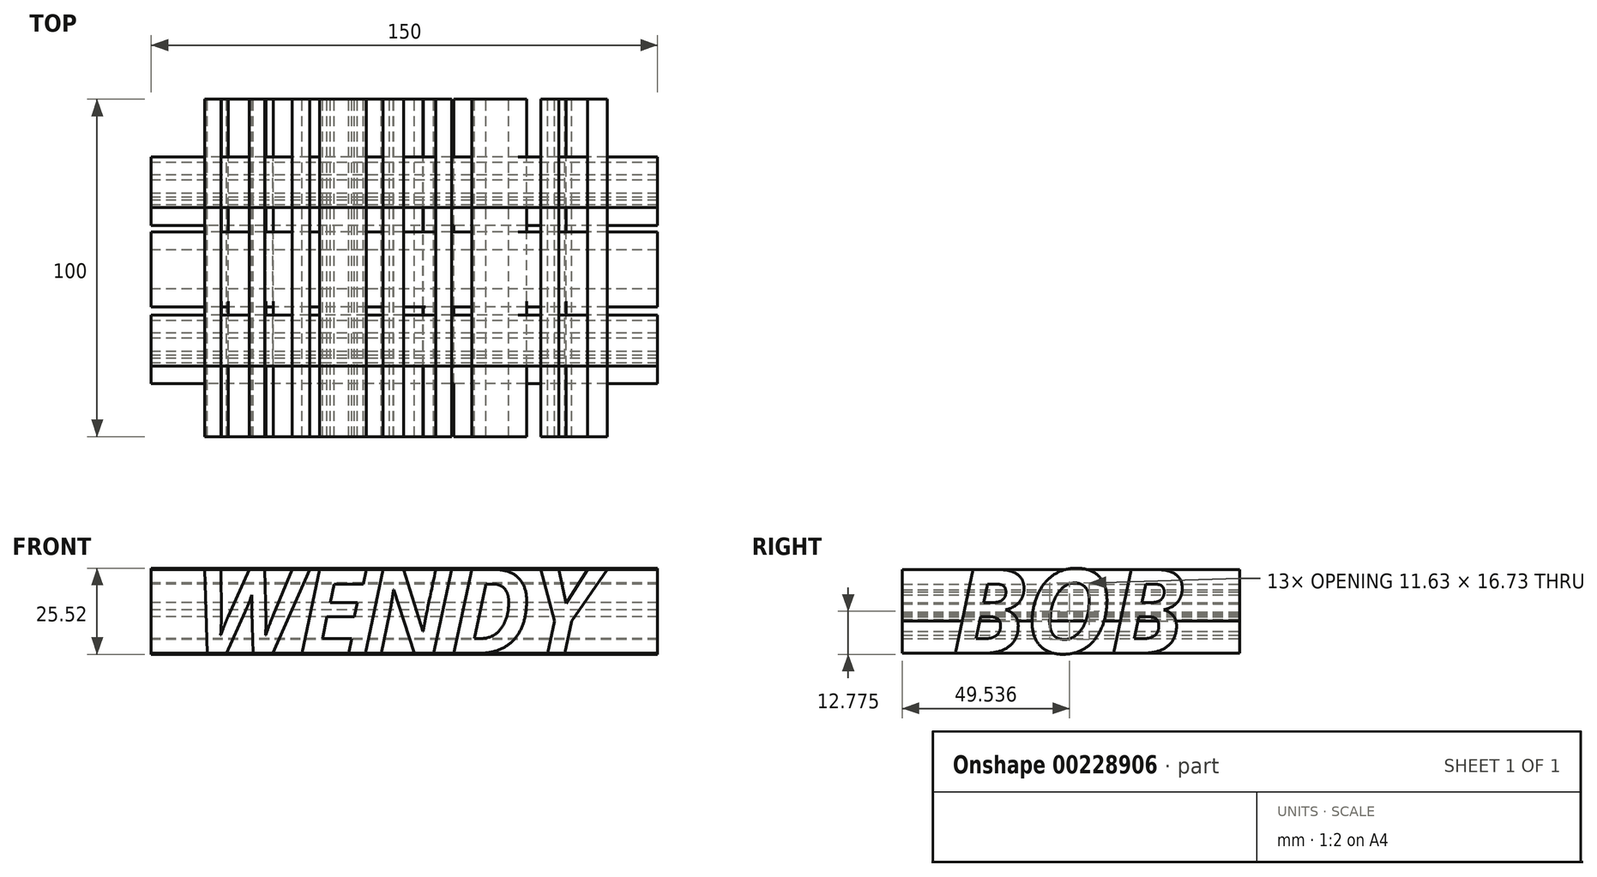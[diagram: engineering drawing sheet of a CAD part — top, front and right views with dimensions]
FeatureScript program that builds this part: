
annotation { "Feature Type Name" : "Feature", "Feature Type Description" : "" }
export const myFeature = defineFeature(function(context is Context, id is Id, definition is map)
    precondition{}
    {
        {
            var Q0;
            Q0=qCreatedBy(makeId("Front.planeOp"),FACE);
            var sketch = newSketch(context, id + "F0", { "sketchPlane" : qUnion([Q0])});
            skText(sketch, "E0", { "text": "WENDY", "fontName": "OpenSans-BoldItalic.ttf"});
            skCircle(sketch, "E1", {"center": v(57.85, 11.4) * mm, "radius": 1.86 * mm});
            const initialGuessF0  = {"E0": [-0.0623, 0, 1, 0, 0.025]};
            skSetInitialGuess(sketch, initialGuessF0);
            skSolve(sketch);
        }
        {
            var Q0;
            Q0 = qSketchRegion(id + "F0", true);
            extrude(context, id + "F1", {"entities" : qUnion([Q0]), "depth" : 50 * mm, "hasSecondDirection" : true, "secondDirectionOppositeDirection" : true, "secondDirectionDepth" : 50 * mm});
        }
        {
            var Q0;
            Q0=qCreatedBy(makeId("Right.planeOp"),FACE);
            var sketch = newSketch(context, id + "F2", { "sketchPlane" : qUnion([Q0])});
            skText(sketch, "E2", { "text": "BOB", "fontName": "OpenSans-BoldItalic.ttf"});
            skCircle(sketch, "E3", {"center": v(38.46, 20.53) * mm, "radius": 2.28 * mm});
            const initialGuessF2  = {"E2": [-0.03517, 0, 1, 0, 0.025]};
            skSetInitialGuess(sketch, initialGuessF2);
            skSolve(sketch);
        }
        {
            var Q0;
            Q0 = qSketchRegion(id + "F2", true);
            extrude(context, id + "F3", {"entities" : qUnion([Q0]), "depth" : 75 * mm, "hasSecondDirection" : true, "secondDirectionOppositeDirection" : true, "secondDirectionDepth" : 75 * mm});
        }
        {
            var Q0;
            Q0=makeQuery(id+"F3.opExtrude","SWEPT_BODY",BODY,{"disambiguationData":[OSD([sQuery(id+"F2.wireOp",EDGE,"E3")])]});
            var Q1;
            Q1=makeQuery(id+"F1.opExtrude","SWEPT_BODY",BODY,{"disambiguationData":[OSD([sQuery(id+"F0.wireOp",EDGE,"E1")])]});
            booleanBodies(context, id + "F4", {"operationType" : BooleanOperationType.INTERSECTION, "tools" : qUnion([Q0, Q1])});
        }
    });
